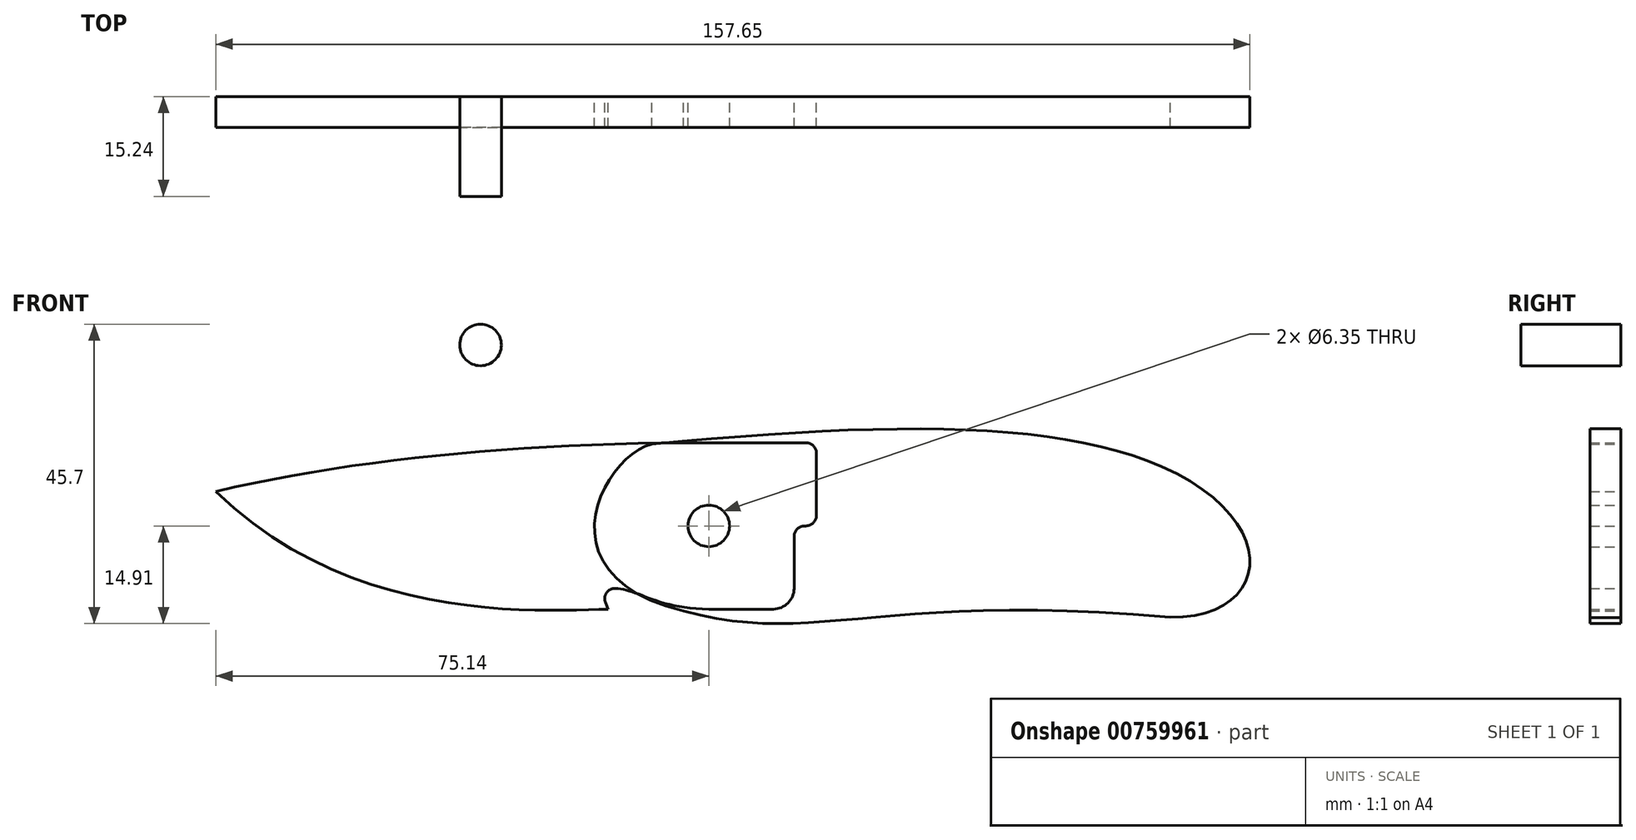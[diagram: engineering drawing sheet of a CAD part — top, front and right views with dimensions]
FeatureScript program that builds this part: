
annotation { "Feature Type Name" : "Feature", "Feature Type Description" : "" }
export const myFeature = defineFeature(function(context is Context, id is Id, definition is map)
    precondition{}
    {
        {
            var Q0;
            Q0=qCreatedBy(makeId("Front.planeOp"),FACE);
            var sketch = newSketch(context, id + "F0", { "sketchPlane" : qUnion([Q0])});
            skCircle(sketch, "E0", {"center": v(0, 0) * mm, "radius": 12.7 * mm, "construction": true});
            skFitSpline(sketch, "E1", {"points": [v(-75.14, 5.26) * mm, v(-14.37, -12.7) * mm], "startDerivative": vector(64.98, -63.76) * mm, "endDerivative": vector(26.44, 0) * mm});
            skFitSpline(sketch, "E2", {"points": [v(0, 12.7) * mm, v(-75.14, 5.26) * mm], "startDerivative": vector(-83.33, 0) * mm, "endDerivative": vector(-64.37, -15.18) * mm});
            skLineSegment(sketch, "E3", {"start": v(14.82, 12.7) * mm, "end": v(0, 12.7) * mm});
            skArc(sketch, "E4", {"start": v(-14.29, -9.53) * mm, "mid": v(-15.6, -10.22) * mm, "end": v(-15.76, -11.7) * mm});
            skLineSegment(sketch, "E5", {"start": v(-12.7, 0) * mm, "end": v(-12.7, -17.94) * mm, "construction": true});
            skLineSegment(sketch, "E6", {"start": v(0, -12.7) * mm, "end": v(-11.7, -12.7) * mm, "construction": true});
            skLineSegment(sketch, "E7", {"start": v(0, -12.7) * mm, "end": v(0, -12.7) * mm});
            skFitSpline(sketch, "E8", {"points": [v(-14.29, -9.52) * mm, v(0, -12.7) * mm], "startDerivative": vector(9.7, 0) * mm, "endDerivative": vector(23.64, 0) * mm});
            skLineSegment(sketch, "E9", {"start": v(-15.36, -12.7) * mm, "end": v(-15.76, -11.7) * mm});
            skArc(sketch, "E10", {"start": v(0, -12.7) * mm, "mid": v(8.98, -8.98) * mm, "end": v(12.7, 0) * mm});
            skCircle(sketch, "E11", {"center": v(0, 0) * mm, "radius": 3.18 * mm});
            skLineSegment(sketch, "E12", {"start": v(0, -12.7) * mm, "end": v(9.84, -12.7) * mm});
            skPoint(sketch, "E13.visualSharp", {"position": v(13.96, -12.7) * mm});
            skArc(sketch, "E13.filletArc", {"start": v(9.84, -12.7) * mm, "mid": v(12.08, -11.77) * mm, "end": v(13.01, -9.52) * mm});
            skLineSegment(sketch, "E14", {"start": v(13.01, -9.52) * mm, "end": v(13.01, -1.59) * mm});
            skLineSegment(sketch, "E15", {"start": v(14.6, 0) * mm, "end": v(14.82, 0) * mm});
            skLineSegment(sketch, "E16", {"start": v(16.41, 1.59) * mm, "end": v(16.41, 11.11) * mm});
            skPoint(sketch, "E17.visualSharp", {"position": v(16.41, 0) * mm});
            skArc(sketch, "E17.filletArc", {"start": v(14.82, 0) * mm, "mid": v(15.95, 0.46) * mm, "end": v(16.41, 1.59) * mm});
            skPoint(sketch, "E18.visualSharp", {"position": v(13.01, 0) * mm});
            skArc(sketch, "E18.filletArc", {"start": v(14.6, 0) * mm, "mid": v(13.48, -0.46) * mm, "end": v(13.01, -1.59) * mm});
            skPoint(sketch, "E19.visualSharp", {"position": v(16.41, 12.7) * mm});
            skArc(sketch, "E19.filletArc", {"start": v(16.41, 11.11) * mm, "mid": v(15.95, 12.24) * mm, "end": v(14.82, 12.7) * mm});
            skSolve(sketch);
        }
        {
            var Q0;
            Q0 = qSketchRegion(id + "F0", true);
            extrude(context, id + "F1", {"entities" : qUnion([Q0]), "depth" : 4.75 * mm, "offsetDistance" : 25.4 * mm});
        }
        {
            var Q0;
            Q0=qCreatedBy(makeId("Front.planeOp"),FACE);
            var sketch = newSketch(context, id + "F2", { "sketchPlane" : qUnion([Q0])});
            skFitSpline(sketch, "E20", {"points": [v(-8.7, 12.47) * mm, v(69.06, 9.04) * mm], "startDerivative": vector(107.63, 10.3) * mm, "endDerivative": vector(48.9, -21.4) * mm});
            skFitSpline(sketch, "E21", {"points": [v(-3.84, -12.97) * mm, v(70.35, -13.97) * mm], "startDerivative": vector(60.03, -16.72) * mm, "endDerivative": vector(133.16, -12.14) * mm});
            skFitSpline(sketch, "E22", {"points": [v(69.06, 9.04) * mm, v(70.35, -13.97) * mm], "startDerivative": vector(55.49, -24.17) * mm, "endDerivative": vector(-46.95, 0.4) * mm});
            skFitSpline(sketch, "E23", {"points": [v(-8.7, 12.47) * mm, v(-3.84, -12.97) * mm], "startDerivative": vector(-22.3, -5.57) * mm, "endDerivative": vector(66.47, -15.87) * mm});
            skCircle(sketch, "E24", {"center": v(0, 0) * mm, "radius": 3.18 * mm});
            skSolve(sketch);
        }
        {
            var Q0;
            Q0=makeQuery(id+"F2.imprint","IMPRINT",FACE,{"disambiguationData":[TD([[makeQuery(id+"F2.imprint","IMPRINT",EDGE,{"derivedFrom":sQuery(id+"F2.wireOp",EDGE,"E20")}),-1.0]])]});
            extrude(context, id + "F3", {"entities" : qUnion([Q0]), "depth" : 4.75 * mm, "offsetDistance" : 25.4 * mm});
        }
        {
            var Q0;
            Q0=qCreatedBy(makeId("Front.planeOp"),FACE);
            var sketch = newSketch(context, id + "F4", { "sketchPlane" : qUnion([Q0])});
            skCircle(sketch, "E25", {"center": v(-34.8, 27.61) * mm, "radius": 3.18 * mm});
            skSolve(sketch);
        }
        {
            var Q0;
            Q0 = qSketchRegion(id + "F4", true);
            extrude(context, id + "F5", {"entities" : qUnion([Q0]), "depth" : 15.24 * mm, "offsetDistance" : 25.4 * mm});
        }
    });
